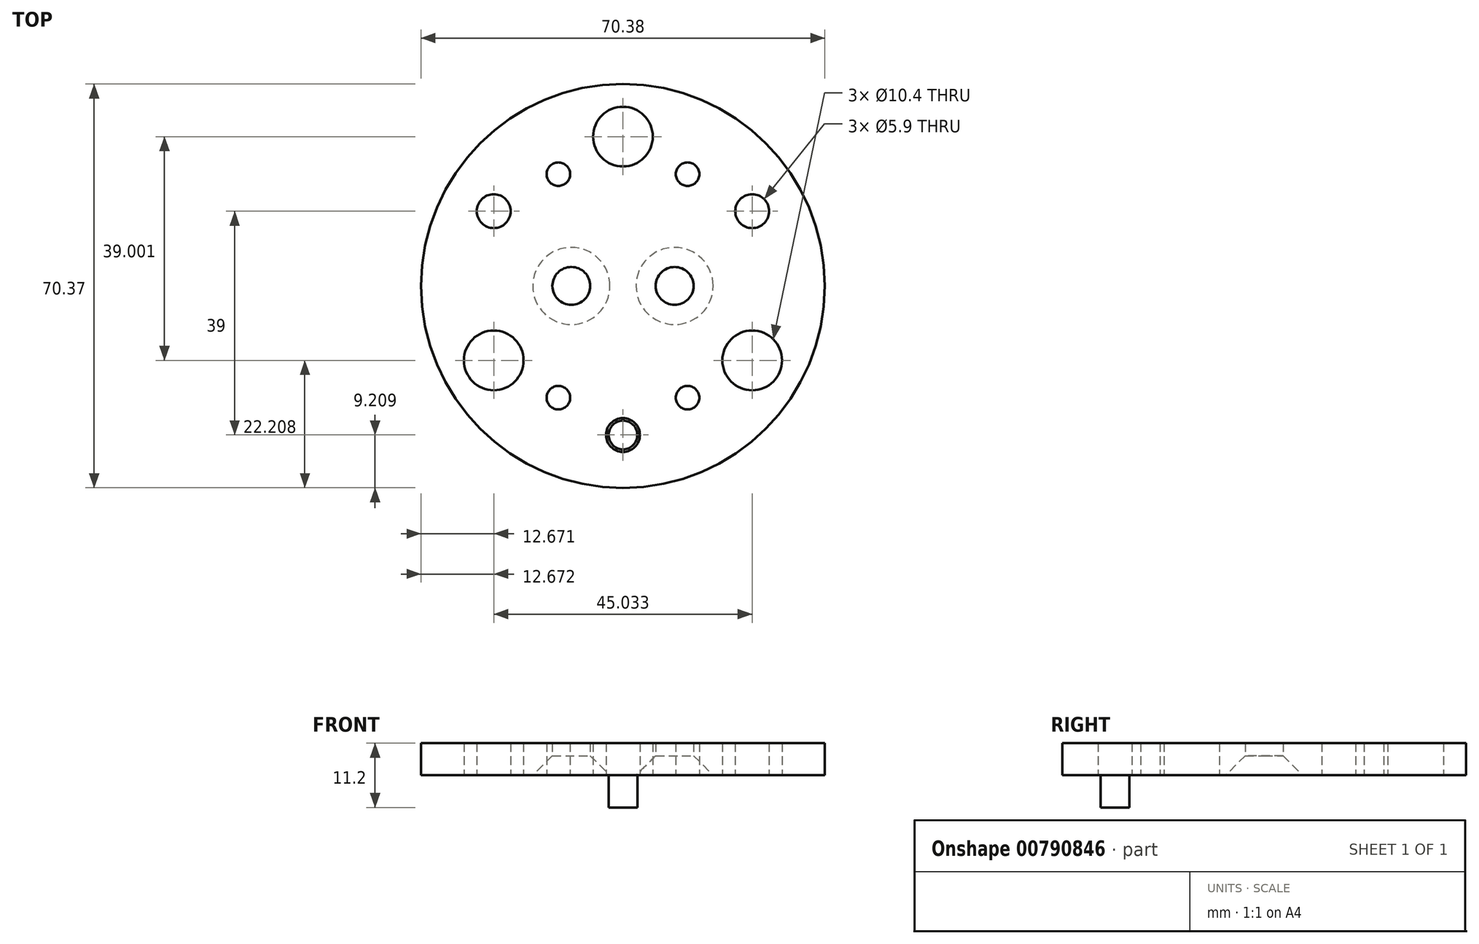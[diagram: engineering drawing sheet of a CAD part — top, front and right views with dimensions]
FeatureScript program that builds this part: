
annotation { "Feature Type Name" : "Feature", "Feature Type Description" : "" }
export const myFeature = defineFeature(function(context is Context, id is Id, definition is map)
    precondition{}
    {
        {
            var Q0;
            Q0=qCreatedBy(makeId("Top.planeOp"),FACE);
            var sketch = newSketch(context, id + "F0", { "sketchPlane" : qUnion([Q0])});
            skCircle(sketch, "E0", {"center": v(11.35, -116.73) * mm, "radius": 3 * mm, "construction": true});
            skCircle(sketch, "E1", {"center": v(56.38, -90.73) * mm, "radius": 2.5 * mm, "construction": true});
            skCircle(sketch, "E2", {"center": v(11.35, -90.73) * mm, "radius": 2.5 * mm, "construction": true});
            skCircle(sketch, "E3", {"center": v(56.38, -116.73) * mm, "radius": 3 * mm, "construction": true});
            skCircle(sketch, "E4", {"center": v(33.86, -77.73) * mm, "radius": 3 * mm, "construction": true});
            skCircle(sketch, "E5", {"center": v(33.86, -129.73) * mm, "radius": 2.5 * mm, "construction": true});
            skCircle(sketch, "E6", {"center": v(33.86, -103.75) * mm, "radius": 32.5 * mm, "construction": true});
            skCircle(sketch, "E7", {"center": v(33.86, -103.75) * mm, "radius": 5.65 * mm, "construction": true});
            skCircle(sketch, "E8", {"center": v(-67.17, -43.32) * mm, "radius": 2.5 * mm});
            skCircle(sketch, "E9", {"center": v(-67.17, 8.68) * mm, "radius": 3 * mm});
            skCircle(sketch, "E10", {"center": v(-44.66, -30.32) * mm, "radius": 3 * mm});
            skCircle(sketch, "E11", {"center": v(-89.69, -4.32) * mm, "radius": 2.5 * mm});
            skCircle(sketch, "E12", {"center": v(-44.66, -4.32) * mm, "radius": 2.5 * mm});
            skCircle(sketch, "E13", {"center": v(-89.69, -30.32) * mm, "radius": 3 * mm});
            skCircle(sketch, "E14", {"center": v(-67.17, -17.35) * mm, "radius": 32.5 * mm});
            skCircle(sketch, "E15", {"center": v(-67.17, -17.35) * mm, "radius": 5.45 * mm});
            skLineSegment(sketch, "E16", {"start": v(0, 0) * mm, "end": v(425.84, 0) * mm, "construction": true});
            skLineSegment(sketch, "E17", {"start": v(0, 0) * mm, "end": v(0, 63.51) * mm, "construction": true});
            skLineSegment(sketch, "E18", {"start": v(-67.17, -17.35) * mm, "end": v(-67.17, 8.68) * mm, "construction": true});
            skSolve(sketch);
        }
        {
            var Q0;
            Q0=makeQuery(id+"F0.imprint","IMPRINT",FACE,{"disambiguationData":[TD([[makeQuery(id+"F0.imprint","IMPRINT",EDGE,{"derivedFrom":sQuery(id+"F0.wireOp",EDGE,"E8")}),1.0]])]});
            extrude(context, id + "F1", {"entities" : qUnion([Q0]), "depth" : 5.6 * mm, "offsetDistance" : 25 * mm});
        }
        {
            var Q0;
            Q0=makeQuery(id+"F1.opExtrude","CAP_FACE",FACE,{"disambiguationData":[OSD([sQuery(id+"F0.wireOp",EDGE,"E8"),sQuery(id+"F0.wireOp",EDGE,"E9"),sQuery(id+"F0.wireOp",EDGE,"E10"),sQuery(id+"F0.wireOp",EDGE,"E11"),sQuery(id+"F0.wireOp",EDGE,"E12"),sQuery(id+"F0.wireOp",EDGE,"E13"),sQuery(id+"F0.wireOp",EDGE,"E14"),sQuery(id+"F0.wireOp",EDGE,"E15")])],"isStart":false});
            var sketch = newSketch(context, id + "F2", { "sketchPlane" : qUnion([Q0])});
            skCircle(sketch, "E19", {"center": v(-89.69, -4.32) * mm, "radius": 2.95 * mm});
            skCircle(sketch, "E20", {"center": v(-44.66, -4.32) * mm, "radius": 2.95 * mm});
            skCircle(sketch, "E21", {"center": v(-67.17, -43.32) * mm, "radius": 2.95 * mm});
            skCircle(sketch, "E22", {"center": v(-67.17, 8.68) * mm, "radius": 5.2 * mm});
            skCircle(sketch, "E23", {"center": v(-89.69, -30.32) * mm, "radius": 5.2 * mm});
            skCircle(sketch, "E24", {"center": v(-44.66, -30.32) * mm, "radius": 5.2 * mm});
            skCircle(sketch, "E25", {"center": v(-67.17, -17.35) * mm, "radius": 35.19 * mm});
            skLineSegment(sketch, "E26", {"start": v(-67.17, -17.35) * mm, "end": v(-21.53, -17.35) * mm, "construction": true});
            skLineSegment(sketch, "E27", {"start": v(-67.17, -17.35) * mm, "end": v(-67.17, 24.88) * mm, "construction": true});
            skPoint(sketch, "E28", {"position": v(-58.17, -17.35) * mm});
            skPoint(sketch, "E29.MirrorP", {"position": v(-76.17, -17.35) * mm});
            skLineSegment(sketch, "E30", {"start": v(-89.69, -30.32) * mm, "end": v(-67.17, -43.32) * mm, "construction": true});
            skLineSegment(sketch, "E31", {"start": v(-67.17, -43.32) * mm, "end": v(-44.66, -30.32) * mm, "construction": true});
            skCircle(sketch, "E32", {"center": v(-55.91, -36.82) * mm, "radius": 2.05 * mm});
            skCircle(sketch, "E33", {"center": v(-78.43, -36.82) * mm, "radius": 2.05 * mm});
            skCircle(sketch, "E34.MirrorC", {"center": v(-78.43, 2.13) * mm, "radius": 2.05 * mm});
            skCircle(sketch, "E35.MirrorC", {"center": v(-55.91, 2.13) * mm, "radius": 2.05 * mm});
            skSolve(sketch);
        }
        {
            var Q0;
            Q0 = qSketchRegion(id + "F2", true);
            extrude(context, id + "F3", {"entities" : qUnion([Q0]), "depth" : 5.6 * mm, "offsetDistance" : 25 * mm});
        }
        {
            var Q0;
            Q0=makeQuery(id+"F3.opExtrude","CAP_FACE",FACE,{"disambiguationData":[OSD([sQuery(id+"F2.wireOp",EDGE,"E19"),sQuery(id+"F2.wireOp",EDGE,"E20"),sQuery(id+"F2.wireOp",EDGE,"E21"),sQuery(id+"F2.wireOp",EDGE,"E22"),sQuery(id+"F2.wireOp",EDGE,"E23"),sQuery(id+"F2.wireOp",EDGE,"E24"),sQuery(id+"F2.wireOp",EDGE,"E25")])],"isStart":true});
            var sketch = newSketch(context, id + "F4", { "sketchPlane" : qUnion([Q0])});
            skLineSegment(sketch, "E36", {"start": v(-67.17, 17.35) * mm, "end": v(-14.26, 17.35) * mm, "construction": true});
            skLineSegment(sketch, "E37", {"start": v(-67.17, 17.35) * mm, "end": v(-67.17, 56.86) * mm, "construction": true});
            skPoint(sketch, "E38", {"position": v(-58.17, 17.35) * mm});
            skPoint(sketch, "E39.MirrorP", {"position": v(-76.17, 17.35) * mm});
            skSolve(sketch);
        }
        {
            var Q0;
            Q0=sQuery(id+"F4.wireOp",VERTEX,"E39.MirrorP");
            var Q1;
            Q1=sQuery(id+"F4.wireOp",VERTEX,"E38");
            var Q2;
            Q2=makeQuery(id+"F3.opExtrude","SWEPT_BODY",BODY,{"disambiguationData":[OSD([sQuery(id+"F2.wireOp",EDGE,"E19"),sQuery(id+"F2.wireOp",EDGE,"E20"),sQuery(id+"F2.wireOp",EDGE,"E21"),sQuery(id+"F2.wireOp",EDGE,"E22"),sQuery(id+"F2.wireOp",EDGE,"E23"),sQuery(id+"F2.wireOp",EDGE,"E24"),sQuery(id+"F2.wireOp",EDGE,"E25")])]});
            hole(context, id + "F5", {"style" : HoleStyle.C_SINK, "endStyle" : HoleEndStyle.THROUGH, "standardTappedOrClearance" : lookupTablePath({ "standard" : "ISO", "fit" : "Normal", "size" : "M6", "type" : "Clearance" }), "standardBlindInLast" : lookupTablePath({ "fit" : "Standard", "standard" : "ISO", "size" : "M6", "type" : "Clearance" }), "holeDiameter" : 6.6 * mm, "cSinkDiameter" : 13.44 * mm, "cSinkAngle" : 90 * degree, "majorDiameter" : 6 * mm, "isTappedThrough" : true, "tappedDepth" : 12 * mm, "tapClearance" : 3, "locations" : qUnion([Q0, Q1]), "scope" : qUnion([Q2])});
        }
    });
